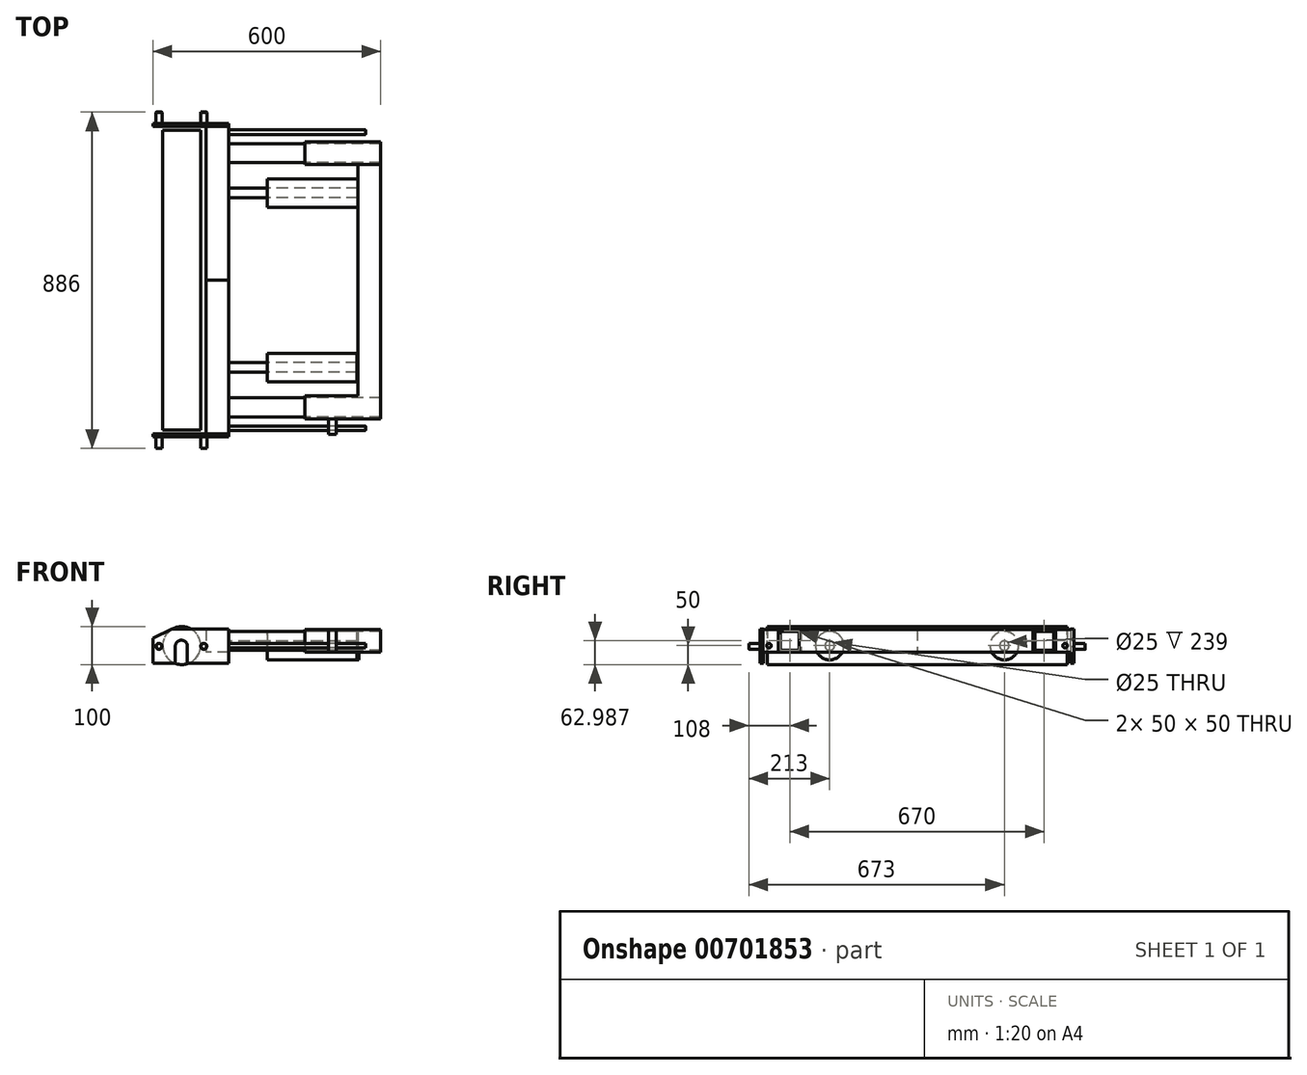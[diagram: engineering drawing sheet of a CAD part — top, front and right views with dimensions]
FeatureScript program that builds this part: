
annotation { "Feature Type Name" : "Feature", "Feature Type Description" : "" }
export const myFeature = defineFeature(function(context is Context, id is Id, definition is map)
    precondition{}
    {
        {
            var Q0;
            Q0=qCreatedBy(makeId("Front.planeOp"),FACE);
            var sketch = newSketch(context, id + "F0", { "sketchPlane" : qUnion([Q0])});
            skLineSegment(sketch, "E0", {"start": v(-17.41, 43.23) * mm, "end": v(132.59, 43.23) * mm});
            skLineSegment(sketch, "E1", {"start": v(132.59, 43.23) * mm, "end": v(132.59, -46.77) * mm});
            skLineSegment(sketch, "E2", {"start": v(-67.41, -46.01) * mm, "end": v(-67.41, 18.99) * mm});
            skArc(sketch, "E3", {"start": v(23.57, -2.59) * mm, "mid": v(7.59, 14.23) * mm, "end": v(-8.4, -2.59) * mm});
            skLineSegment(sketch, "E4", {"start": v(-67.41, -46.01) * mm, "end": v(-8.4, -46.01) * mm});
            skLineSegment(sketch, "E5", {"start": v(-17.41, 43.23) * mm, "end": v(-67.41, 18.99) * mm});
            skLineSegment(sketch, "E6", {"start": v(-8.4, -2.59) * mm, "end": v(-8.4, -46.01) * mm});
            skLineSegment(sketch, "E7", {"start": v(23.57, -2.59) * mm, "end": v(23.57, -46.01) * mm});
            skLineSegment(sketch, "E8.trimOffspring", {"start": v(23.57, -46.01) * mm, "end": v(134.26, -46.01) * mm});
            skPoint(sketch, "E9.orphan", {"position": v(-67.41, 43.23) * mm});
            skSolve(sketch);
        }
        {
            var Q0;
            {var subQ1=sQuery(id+"F0.wireOp",EDGE,"E0");Q0=makeQuery(id+"F0.imprint","IMPRINT",FACE,{"disambiguationData":[TD([[makeQuery(id+"F0.imprint","IMPRINT",EDGE,{"derivedFrom":subQ1}),-1.0]])]});}
            extrude(context, id + "F1", {"entities" : qUnion([Q0]), "oppositeDirection" : true, "depth" : 8 * mm, "offsetDistance" : 25 * mm});
        }
        {
            var Q0;
            Q0=makeQuery(id+"F1.opExtrude","CAP_FACE",FACE,{"disambiguationData":[OSD([sQuery(id+"F0.wireOp",EDGE,"E0"),sQuery(id+"F0.wireOp",EDGE,"E1"),sQuery(id+"F0.wireOp",EDGE,"E2"),sQuery(id+"F0.wireOp",EDGE,"E3"),sQuery(id+"F0.wireOp",EDGE,"E4"),sQuery(id+"F0.wireOp",EDGE,"E5"),sQuery(id+"F0.wireOp",EDGE,"E6"),sQuery(id+"F0.wireOp",EDGE,"E7"),sQuery(id+"F0.wireOp",EDGE,"E8.trimOffspring")])],"isStart":true});
            var sketch = newSketch(context, id + "F2", { "sketchPlane" : qUnion([Q0])});
            skCircle(sketch, "E10", {"center": v(-51.41, -1.77) * mm, "radius": 8 * mm});
            skCircle(sketch, "E11", {"center": v(66.59, -1.77) * mm, "radius": 8 * mm});
            skSolve(sketch);
        }
        {
            var Q0;
            Q0=makeQuery(id+"F2.imprint","IMPRINT",FACE,{"disambiguationData":[TD([[makeQuery(id+"F2.imprint","IMPRINT",EDGE,{"derivedFrom":sQuery(id+"F2.wireOp",EDGE,"E10")}),1.0]])]});
            var Q1;
            Q1=makeQuery(id+"F2.imprint","IMPRINT",FACE,{"disambiguationData":[TD([[makeQuery(id+"F2.imprint","IMPRINT",EDGE,{"derivedFrom":sQuery(id+"F2.wireOp",EDGE,"E11")}),1.0]])]});
            extrude(context, id + "F3", {"entities" : qUnion([Q0, Q1]), "operationType" : NewBodyOperationType.ADD, "depth" : 30 * mm, "offsetDistance" : 25 * mm});
        }
        {
            var Q0;
            Q0=makeQuery(id+"F3.opExtrude","CAP_EDGE",EDGE,{"disambiguationData":[OSD([sQuery(id+"F2.wireOp",EDGE,"E10")])],"isStart":false});
            var Q1;
            Q1=makeQuery(id+"F3.opExtrude","CAP_FACE",FACE,{"disambiguationData":[OSD([sQuery(id+"F2.wireOp",EDGE,"E11")])],"isStart":false});
            chamfer(context, id + "F4", {"entities" : qUnion([Q0, Q1]), "width" : 0.5 * mm, "tangentPropagation" : true});
        }
        {
            var Q0;
            Q0=makeQuery(id+"F1.opExtrude","CAP_FACE",FACE,{"disambiguationData":[OSD([sQuery(id+"F0.wireOp",EDGE,"E0"),sQuery(id+"F0.wireOp",EDGE,"E1"),sQuery(id+"F0.wireOp",EDGE,"E2"),sQuery(id+"F0.wireOp",EDGE,"E3"),sQuery(id+"F0.wireOp",EDGE,"E4"),sQuery(id+"F0.wireOp",EDGE,"E5"),sQuery(id+"F0.wireOp",EDGE,"E6"),sQuery(id+"F0.wireOp",EDGE,"E7"),sQuery(id+"F0.wireOp",EDGE,"E8.trimOffspring")])],"isStart":false});
            var sketch = newSketch(context, id + "F5", { "sketchPlane" : qUnion([Q0])});
            skLineSegment(sketch, "E12.bottom", {"start": v(-132.59, 42.99) * mm, "end": v(-72.59, 42.99) * mm});
            skLineSegment(sketch, "E12.top", {"start": v(-132.59, -17.01) * mm, "end": v(-72.59, -17.01) * mm});
            skLineSegment(sketch, "E12.left", {"start": v(-132.59, 42.99) * mm, "end": v(-132.59, -17.01) * mm});
            skLineSegment(sketch, "E12.right", {"start": v(-72.59, 42.99) * mm, "end": v(-72.59, -17.01) * mm});
            skSolve(sketch);
        }
        {
            var Q0;
            Q0=makeQuery(id+"F5.imprint","IMPRINT",FACE,{"disambiguationData":[TD([[makeQuery(id+"F5.imprint","IMPRINT",EDGE,{"derivedFrom":sQuery(id+"F5.wireOp",EDGE,"E12.bottom")}),-1.0]])]});
            extrude(context, id + "F6", {"entities" : qUnion([Q0]), "operationType" : NewBodyOperationType.ADD, "depth" : 405 * mm, "offsetDistance" : 25 * mm});
        }
        {
            var Q0;
            {var subQ0=makeQuery(id+"F6.boolean.opBoolean","MERGE",FACE,{"derivedFrom":[makeQuery(id+"F1.opExtrude","SWEPT_FACE",FACE,{"disambiguationData":[OSD([sQuery(id+"F0.wireOp",EDGE,"E1")])]}),makeQuery(id+"F6.opExtrude","SWEPT_FACE",FACE,{"disambiguationData":[OSD([sQuery(id+"F5.wireOp",EDGE,"E12.left")])]})]});Q0=makeQuery(id+"F12.boolean.opBoolean","MERGE",FACE,{"derivedFrom":[subQ0,makeQuery(id+"F12.opPattern","COPY",FACE,{"derivedFrom":subQ0,"instanceName":"1"})]});}
            var sketch = newSketch(context, id + "F7", { "sketchPlane" : qUnion([Q0])});
            skLineSegment(sketch, "E13.bottom", {"start": v(53, 37.99) * mm, "end": v(103, 37.99) * mm});
            skLineSegment(sketch, "E13.top", {"start": v(53, -12.01) * mm, "end": v(103, -12.01) * mm});
            skLineSegment(sketch, "E13.left", {"start": v(53, 37.99) * mm, "end": v(53, -12.01) * mm});
            skLineSegment(sketch, "E13.right", {"start": v(103, 37.99) * mm, "end": v(103, -12.01) * mm});
            skSolve(sketch);
        }
        {
            var Q0;
            Q0=makeQuery(id+"F7.imprint","IMPRINT",FACE,{"disambiguationData":[TD([[makeQuery(id+"F7.imprint","IMPRINT",EDGE,{"derivedFrom":sQuery(id+"F7.wireOp",EDGE,"E13.bottom")}),-1.0]])]});
            extrude(context, id + "F8", {"entities" : qUnion([Q0]), "operationType" : NewBodyOperationType.ADD, "depth" : 200 * mm, "offsetDistance" : 25 * mm});
        }
        {
            var Q0;
            Q0=makeQuery(id+"F8.opExtrude","CAP_FACE",FACE,{"disambiguationData":[OSD([sQuery(id+"F7.wireOp",EDGE,"E13.bottom"),sQuery(id+"F7.wireOp",EDGE,"E13.top"),sQuery(id+"F7.wireOp",EDGE,"E13.left"),sQuery(id+"F7.wireOp",EDGE,"E13.right")])],"isStart":false});
            var sketch = newSketch(context, id + "F9", { "sketchPlane" : qUnion([Q0])});
            skLineSegment(sketch, "E14", {"start": v(53, 37.99) * mm, "end": v(772.6, 37.99) * mm});
            skSolve(sketch);
        }
        {
            var Q0;
            Q0=makeQuery(id+"F9.imprint","IMPRINT",FACE,{"disambiguationData":[TD([[makeQuery(id+"F9.imprint","IMPRINT",EDGE,{"derivedFrom":makeQuery(id+"F8.opExtrude","CAP_EDGE",EDGE,{"disambiguationData":[OSD([sQuery(id+"F7.wireOp",EDGE,"E13.top")])],"isStart":false})}),1.0]])]});
            var sketch = newSketch(context, id + "F10", { "sketchPlane" : qUnion([Q0])});
            skLineSegment(sketch, "E15.bottom", {"start": v(48, 42.99) * mm, "end": v(108, 42.99) * mm});
            skLineSegment(sketch, "E15.top", {"start": v(48, -17.01) * mm, "end": v(108, -17.01) * mm});
            skLineSegment(sketch, "E15.left", {"start": v(48, 42.99) * mm, "end": v(48, -17.01) * mm});
            skLineSegment(sketch, "E15.right", {"start": v(108, 42.99) * mm, "end": v(108, -17.01) * mm});
            skSolve(sketch);
        }
        {
            var Q0;
            Q0=makeQuery(id+"F10.imprint","IMPRINT",FACE,{"disambiguationData":[TD([[makeQuery(id+"F10.imprint","IMPRINT",EDGE,{"derivedFrom":sQuery(id+"F10.wireOp",EDGE,"E15.bottom")}),-1.0]])]});
            extrude(context, id + "F11", {"entities" : qUnion([Q0]), "depth" : 200 * mm, "offsetDistance" : 25 * mm});
        }
        {
            var Q0;
            Q0=makeQuery(id+"F1.opExtrude","SWEPT_BODY",BODY,{"disambiguationData":[OSD([sQuery(id+"F0.wireOp",EDGE,"E0"),sQuery(id+"F0.wireOp",EDGE,"E1"),sQuery(id+"F0.wireOp",EDGE,"E2"),sQuery(id+"F0.wireOp",EDGE,"E3"),sQuery(id+"F0.wireOp",EDGE,"E4"),sQuery(id+"F0.wireOp",EDGE,"E5"),sQuery(id+"F0.wireOp",EDGE,"E6"),sQuery(id+"F0.wireOp",EDGE,"E7"),sQuery(id+"F0.wireOp",EDGE,"E8.trimOffspring")])]});
            var Q1;
            Q1=makeQuery(id+"F6.opExtrude","CAP_FACE",FACE,{"disambiguationData":[OSD([sQuery(id+"F5.wireOp",EDGE,"E12.bottom"),sQuery(id+"F5.wireOp",EDGE,"E12.top"),sQuery(id+"F5.wireOp",EDGE,"E12.left"),sQuery(id+"F5.wireOp",EDGE,"E12.right")])],"isStart":false});
            mirror(context, id + "F12", {"operationType" : NewBodyOperationType.ADD, "entities" : qUnion([Q0]), "mirrorPlane" : qUnion([Q1])});
        }
        {
            var Q0;
            Q0=makeQuery(id+"F11.opExtrude","SWEPT_FACE",FACE,{"disambiguationData":[OSD([sQuery(id+"F10.wireOp",EDGE,"E15.right")])]});
            var sketch = newSketch(context, id + "F13", { "sketchPlane" : qUnion([Q0])});
            skLineSegment(sketch, "E16.bottom", {"start": v(-532.59, 42.99) * mm, "end": v(-472.59, 42.99) * mm});
            skLineSegment(sketch, "E16.top", {"start": v(-532.59, -17.01) * mm, "end": v(-472.59, -17.01) * mm});
            skLineSegment(sketch, "E16.left", {"start": v(-532.59, 42.99) * mm, "end": v(-532.59, -17.01) * mm});
            skLineSegment(sketch, "E16.right", {"start": v(-472.59, 42.99) * mm, "end": v(-472.59, -17.01) * mm});
            skSolve(sketch);
        }
        {
            var Q0;
            Q0=makeQuery(id+"F13.imprint","IMPRINT",FACE,{"disambiguationData":[TD([[makeQuery(id+"F13.imprint","IMPRINT",EDGE,{"derivedFrom":sQuery(id+"F13.wireOp",EDGE,"E16.bottom")}),-1.0]])]});
            extrude(context, id + "F14", {"entities" : qUnion([Q0]), "operationType" : NewBodyOperationType.ADD, "depth" : 610 * mm, "offsetDistance" : 25 * mm});
        }
        {
            var Q0;
            Q0=makeQuery(id+"F12.opPattern","COPY",FACE,{"derivedFrom":makeQuery(id+"F8.opExtrude","CAP_FACE",FACE,{"disambiguationData":[OSD([sQuery(id+"F7.wireOp",EDGE,"E13.bottom"),sQuery(id+"F7.wireOp",EDGE,"E13.top"),sQuery(id+"F7.wireOp",EDGE,"E13.left"),sQuery(id+"F7.wireOp",EDGE,"E13.right")])],"isStart":false}),"instanceName":"1"});
            var sketch = newSketch(context, id + "F15", { "sketchPlane" : qUnion([Q0])});
            skLineSegment(sketch, "E17.bottom", {"start": v(718, 42.99) * mm, "end": v(778, 42.99) * mm});
            skLineSegment(sketch, "E17.top", {"start": v(718, -17.01) * mm, "end": v(778, -17.01) * mm});
            skLineSegment(sketch, "E17.left", {"start": v(718, 42.99) * mm, "end": v(718, -17.01) * mm});
            skLineSegment(sketch, "E17.right", {"start": v(778, 42.99) * mm, "end": v(778, -17.01) * mm});
            skSolve(sketch);
        }
        {
            var Q0;
            Q0=makeQuery(id+"F15.imprint","IMPRINT",FACE,{"disambiguationData":[TD([[makeQuery(id+"F15.imprint","IMPRINT",EDGE,{"derivedFrom":sQuery(id+"F15.wireOp",EDGE,"E17.bottom")}),-1.0]])]});
            extrude(context, id + "F16", {"entities" : qUnion([Q0]), "depth" : 200 * mm, "offsetDistance" : 25 * mm});
        }
        {
            var Q0;
            {var subQ0=makeQuery(id+"F6.boolean.opBoolean","MERGE",FACE,{"derivedFrom":[makeQuery(id+"F1.opExtrude","SWEPT_FACE",FACE,{"disambiguationData":[OSD([sQuery(id+"F0.wireOp",EDGE,"E1")])]}),makeQuery(id+"F6.opExtrude","SWEPT_FACE",FACE,{"disambiguationData":[OSD([sQuery(id+"F5.wireOp",EDGE,"E12.left")])]})]});Q0=makeQuery(id+"F12.boolean.opBoolean","MERGE",FACE,{"derivedFrom":[subQ0,makeQuery(id+"F12.opPattern","COPY",FACE,{"derivedFrom":subQ0,"instanceName":"1"})]});}
            var sketch = newSketch(context, id + "F17", { "sketchPlane" : qUnion([Q0])});
            skCircle(sketch, "E18", {"center": v(23, 0) * mm, "radius": 6 * mm});
            skPoint(sketch, "E19.centerSnap0", {"position": v(818, -31.51) * mm});
            skCircle(sketch, "E20", {"center": v(803, 0) * mm, "radius": 6 * mm});
            skSolve(sketch);
        }
        {
            var Q0;
            Q0=makeQuery(id+"F17.imprint","IMPRINT",FACE,{"disambiguationData":[TD([[makeQuery(id+"F17.imprint","IMPRINT",EDGE,{"derivedFrom":sQuery(id+"F17.wireOp",EDGE,"E18")}),1.0]])]});
            extrude(context, id + "F18", {"entities" : qUnion([Q0]), "operationType" : NewBodyOperationType.ADD, "depth" : 360 * mm, "offsetDistance" : 25 * mm});
        }
        {
            var Q0;
            Q0=makeQuery(id+"F17.imprint","IMPRINT",FACE,{"disambiguationData":[TD([[makeQuery(id+"F17.imprint","IMPRINT",EDGE,{"derivedFrom":sQuery(id+"F17.wireOp",EDGE,"E20")}),1.0]])]});
            extrude(context, id + "F19", {"entities" : qUnion([Q0]), "operationType" : NewBodyOperationType.ADD, "depth" : 360 * mm, "offsetDistance" : 25 * mm});
        }
        {
            var Q0;
            Q0=makeQuery(id+"F11.opExtrude","SWEPT_FACE",FACE,{"disambiguationData":[OSD([sQuery(id+"F10.wireOp",EDGE,"E15.left")])]});
            var sketch = newSketch(context, id + "F20", { "sketchPlane" : qUnion([Q0])});
            skLineSegment(sketch, "E21.bottom", {"start": v(395.6, 42.99) * mm, "end": v(415.6, 42.99) * mm});
            skLineSegment(sketch, "E21.top", {"start": v(395.6, -17.01) * mm, "end": v(415.6, -17.01) * mm});
            skLineSegment(sketch, "E21.left", {"start": v(395.6, 42.99) * mm, "end": v(395.6, -17.01) * mm});
            skLineSegment(sketch, "E21.right", {"start": v(415.6, 42.99) * mm, "end": v(415.6, -17.01) * mm});
            skSolve(sketch);
        }
        {
            var Q0;
            Q0=makeQuery(id+"F20.imprint","IMPRINT",FACE,{"disambiguationData":[TD([[makeQuery(id+"F20.imprint","IMPRINT",EDGE,{"derivedFrom":sQuery(id+"F20.wireOp",EDGE,"E21.bottom")}),1.0]])]});
            extrude(context, id + "F21", {"entities" : qUnion([Q0]), "depth" : 41 * mm, "offsetDistance" : 25 * mm});
        }
        {
            var Q0;
            Q0=makeQuery(id+"F17.imprint","IMPRINT",FACE,{"disambiguationData":[TD([[makeQuery(id+"F17.imprint","IMPRINT",EDGE,{"derivedFrom":sQuery(id+"F17.wireOp",EDGE,"E18")}),-1.0]])]});
            var sketch = newSketch(context, id + "F22", { "sketchPlane" : qUnion([Q0])});
            skCircle(sketch, "E22", {"center": v(183, 0) * mm, "radius": 12.5 * mm});
            skSolve(sketch);
        }
        {
            var Q0;
            Q0=makeQuery(id+"F22.imprint","IMPRINT",FACE,{"disambiguationData":[TD([[makeQuery(id+"F22.imprint","IMPRINT",EDGE,{"derivedFrom":sQuery(id+"F22.wireOp",EDGE,"E22")}),1.0]])]});
            extrude(context, id + "F23", {"entities" : qUnion([Q0]), "operationType" : NewBodyOperationType.ADD, "depth" : 101 * mm, "offsetDistance" : 25 * mm});
        }
        {
            var Q0;
            Q0=makeQuery(id+"F23.opExtrude","CAP_FACE",FACE,{"disambiguationData":[OSD([sQuery(id+"F22.wireOp",EDGE,"E22")])],"isStart":false});
            var sketch = newSketch(context, id + "F24", { "sketchPlane" : qUnion([Q0])});
            skCircle(sketch, "E23", {"center": v(183, 0) * mm, "radius": 37.5 * mm});
            skSolve(sketch);
        }
        {
            var Q0;
            Q0=makeQuery(id+"F24.imprint","IMPRINT",FACE,{"disambiguationData":[TD([[makeQuery(id+"F24.imprint","IMPRINT",EDGE,{"derivedFrom":sQuery(id+"F24.wireOp",EDGE,"E23")}),1.0]])]});
            extrude(context, id + "F25", {"entities" : qUnion([Q0]), "depth" : 237 * mm, "offsetDistance" : 25 * mm});
        }
        {
            var Q0;
            Q0=makeQuery(id+"F17.imprint","IMPRINT",FACE,{"disambiguationData":[TD([[makeQuery(id+"F17.imprint","IMPRINT",EDGE,{"derivedFrom":sQuery(id+"F17.wireOp",EDGE,"E18")}),-1.0]])]});
            var sketch = newSketch(context, id + "F26", { "sketchPlane" : qUnion([Q0])});
            skCircle(sketch, "E24", {"center": v(643, 0) * mm, "radius": 12.5 * mm});
            skSolve(sketch);
        }
        {
            var Q0;
            Q0 = qSketchRegion(id + "F26", true);
            extrude(context, id + "F27", {"entities" : qUnion([Q0]), "operationType" : NewBodyOperationType.ADD, "depth" : 101 * mm, "offsetDistance" : 25 * mm});
        }
        {
            var Q0;
            Q0=makeQuery(id+"F27.opExtrude","CAP_FACE",FACE,{"disambiguationData":[OSD([sQuery(id+"F26.wireOp",EDGE,"E24")])],"isStart":false});
            var sketch = newSketch(context, id + "F28", { "sketchPlane" : qUnion([Q0])});
            skCircle(sketch, "E25", {"center": v(643, 0) * mm, "radius": 37.5 * mm});
            skSolve(sketch);
        }
        {
            var Q0;
            Q0=makeQuery(id+"F28.imprint","IMPRINT",FACE,{"disambiguationData":[TD([[makeQuery(id+"F28.imprint","IMPRINT",EDGE,{"derivedFrom":sQuery(id+"F28.wireOp",EDGE,"E25")}),1.0]])]});
            extrude(context, id + "F29", {"entities" : qUnion([Q0]), "operationType" : NewBodyOperationType.ADD, "depth" : 241 * mm, "offsetDistance" : 25 * mm});
        }
        {
            var Q0;
            Q0=makeQuery(id+"F12.opPattern","COPY",FACE,{"derivedFrom":makeQuery(id+"F1.opExtrude","CAP_FACE",FACE,{"disambiguationData":[OSD([sQuery(id+"F0.wireOp",EDGE,"E0"),sQuery(id+"F0.wireOp",EDGE,"E1"),sQuery(id+"F0.wireOp",EDGE,"E2"),sQuery(id+"F0.wireOp",EDGE,"E3"),sQuery(id+"F0.wireOp",EDGE,"E4"),sQuery(id+"F0.wireOp",EDGE,"E5"),sQuery(id+"F0.wireOp",EDGE,"E6"),sQuery(id+"F0.wireOp",EDGE,"E7"),sQuery(id+"F0.wireOp",EDGE,"E8.trimOffspring")])],"isStart":false}),"instanceName":"1"});
            cPlane(context, id + "F30", {"entities" : qUnion([Q0]), "cplaneType" : CPlaneType.OFFSET, "offset" : 10 * mm, "width" : 150 * mm, "height" : 150 * mm});
        }
        {
            var Q0;
            Q0=qCreatedBy(id+"F30.planeOp",FACE);
            var sketch = newSketch(context, id + "F31", { "sketchPlane" : qUnion([Q0])});
            skCircle(sketch, "E26", {"center": v(8.57, 0) * mm, "radius": 50 * mm});
            skSolve(sketch);
        }
        {
            var Q0;
            Q0=makeQuery(id+"F31.imprint","IMPRINT",FACE,{"disambiguationData":[TD([[makeQuery(id+"F31.imprint","IMPRINT",EDGE,{"derivedFrom":sQuery(id+"F31.wireOp",EDGE,"E26")}),1.0]])]});
            extrude(context, id + "F32", {"entities" : qUnion([Q0]), "depth" : 790 * mm, "offsetDistance" : 25 * mm});
        }
    });
